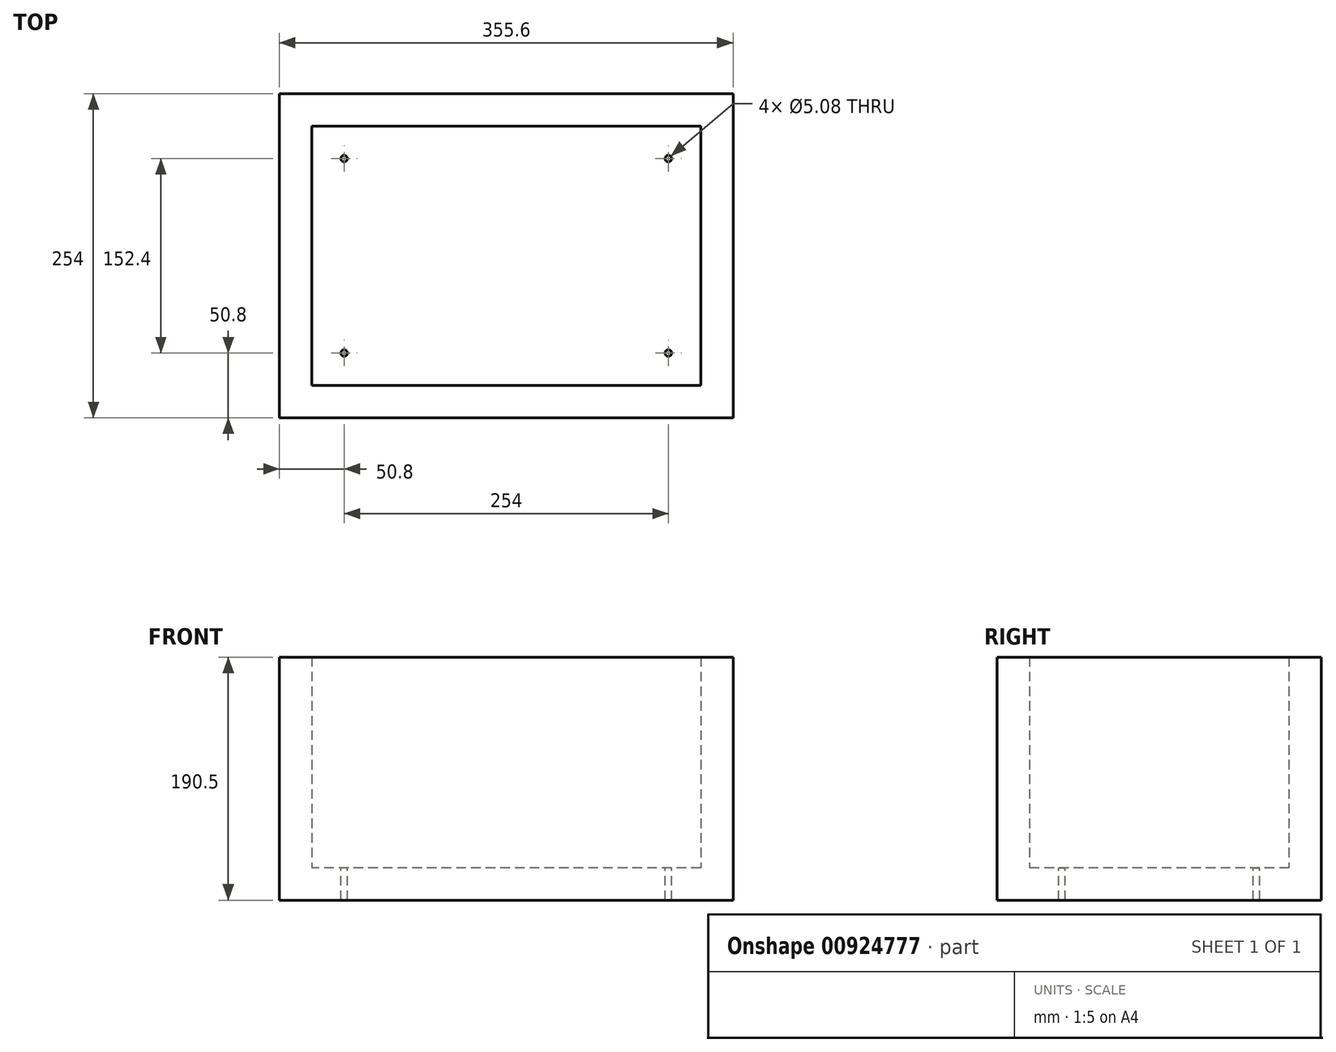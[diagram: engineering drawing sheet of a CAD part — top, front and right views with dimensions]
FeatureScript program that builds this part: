
annotation { "Feature Type Name" : "Feature", "Feature Type Description" : "" }
export const myFeature = defineFeature(function(context is Context, id is Id, definition is map)
    precondition{}
    {
        {
            var Q0;
            Q0=qCreatedBy(makeId("Top.planeOp"),FACE);
            var Q1;
            Q1=qCreatedBy(makeId("Top.planeOp"),FACE);
            var sketch = newSketch(context, id + "F0", { "sketchPlane" : qUnion([Q0, Q1])});
            skLineSegment(sketch, "E0.bottom", {"start": v(177.8, 127) * mm, "end": v(-177.8, 127) * mm});
            skLineSegment(sketch, "E0.top", {"start": v(177.8, -127) * mm, "end": v(-177.8, -127) * mm});
            skLineSegment(sketch, "E0.left", {"start": v(177.8, 127) * mm, "end": v(177.8, -127) * mm});
            skLineSegment(sketch, "E0.right", {"start": v(-177.8, 127) * mm, "end": v(-177.8, -127) * mm});
            skPoint(sketch, "E0.middle", {"position": v(0, 0) * mm});
            skSolve(sketch);
        }
        {
            var Q0;
            Q0 = qSketchRegion(id + "F0", true);
            extrude(context, id + "F1", {"entities" : qUnion([Q0]), "depth" : 190.5 * mm, "offsetDistance" : 25.4 * mm});
        }
        {
            var Q0;
            Q0=makeQuery(id+"F1.opExtrude","CAP_FACE",FACE,{"disambiguationData":[OSD([sQuery(id+"F0.wireOp",EDGE,"E0.bottom"),sQuery(id+"F0.wireOp",EDGE,"E0.top"),sQuery(id+"F0.wireOp",EDGE,"E0.left"),sQuery(id+"F0.wireOp",EDGE,"E0.right")])],"isStart":false});
            shell(context, id + "F2", {"entities" : qUnion([Q0]), "thickness" : 25.4 * mm});
        }
        {
            var Q0;
            Q0=makeQuery(id+"F2.opShell","OFFSET_FACE",FACE,{"disambiguationData":[OSD([sQuery(id+"F0.wireOp",EDGE,"E0.bottom"),sQuery(id+"F0.wireOp",EDGE,"E0.top"),sQuery(id+"F0.wireOp",EDGE,"E0.left"),sQuery(id+"F0.wireOp",EDGE,"E0.right")])]});
            var Q1;
            Q1=makeQuery(id+"F2.opShell","OFFSET_FACE",FACE,{"disambiguationData":[OSD([sQuery(id+"F0.wireOp",EDGE,"E0.bottom"),sQuery(id+"F0.wireOp",EDGE,"E0.top"),sQuery(id+"F0.wireOp",EDGE,"E0.left"),sQuery(id+"F0.wireOp",EDGE,"E0.right")])]});
            var sketch = newSketch(context, id + "F3", { "sketchPlane" : qUnion([Q0, Q1])});
            skPoint(sketch, "E1", {"position": v(-127, 76.2) * mm});
            skPoint(sketch, "E2", {"position": v(127, 76.2) * mm});
            skPoint(sketch, "E3", {"position": v(127, -76.2) * mm});
            skPoint(sketch, "E4", {"position": v(-127, -76.2) * mm});
            skSolve(sketch);
        }
        {
            var Q0;
            Q0=sQuery(id+"F3.wireOp",VERTEX,"E1");
            var Q1;
            Q1=sQuery(id+"F3.wireOp",VERTEX,"E4");
            var Q2;
            Q2=sQuery(id+"F3.wireOp",VERTEX,"E3");
            var Q3;
            Q3=sQuery(id+"F3.wireOp",VERTEX,"E2");
            var Q4;
            Q4=makeQuery(id+"F1.opExtrude","SWEPT_BODY",BODY,{"disambiguationData":[OSD([sQuery(id+"F0.wireOp",EDGE,"E0.bottom"),sQuery(id+"F0.wireOp",EDGE,"E0.top"),sQuery(id+"F0.wireOp",EDGE,"E0.left"),sQuery(id+"F0.wireOp",EDGE,"E0.right")])]});
            hole(context, id + "F4", {"style" : HoleStyle.SIMPLE, "endStyle" : HoleEndStyle.THROUGH, "holeDiameter" : 5.08 * mm, "majorDiameter" : 6.35 * mm, "isTappedThrough" : true, "tappedDepth" : 12.7 * mm, "tapClearance" : 3, "locations" : qUnion([Q0, Q1, Q2, Q3]), "scope" : qUnion([Q4])});
        }
    });
